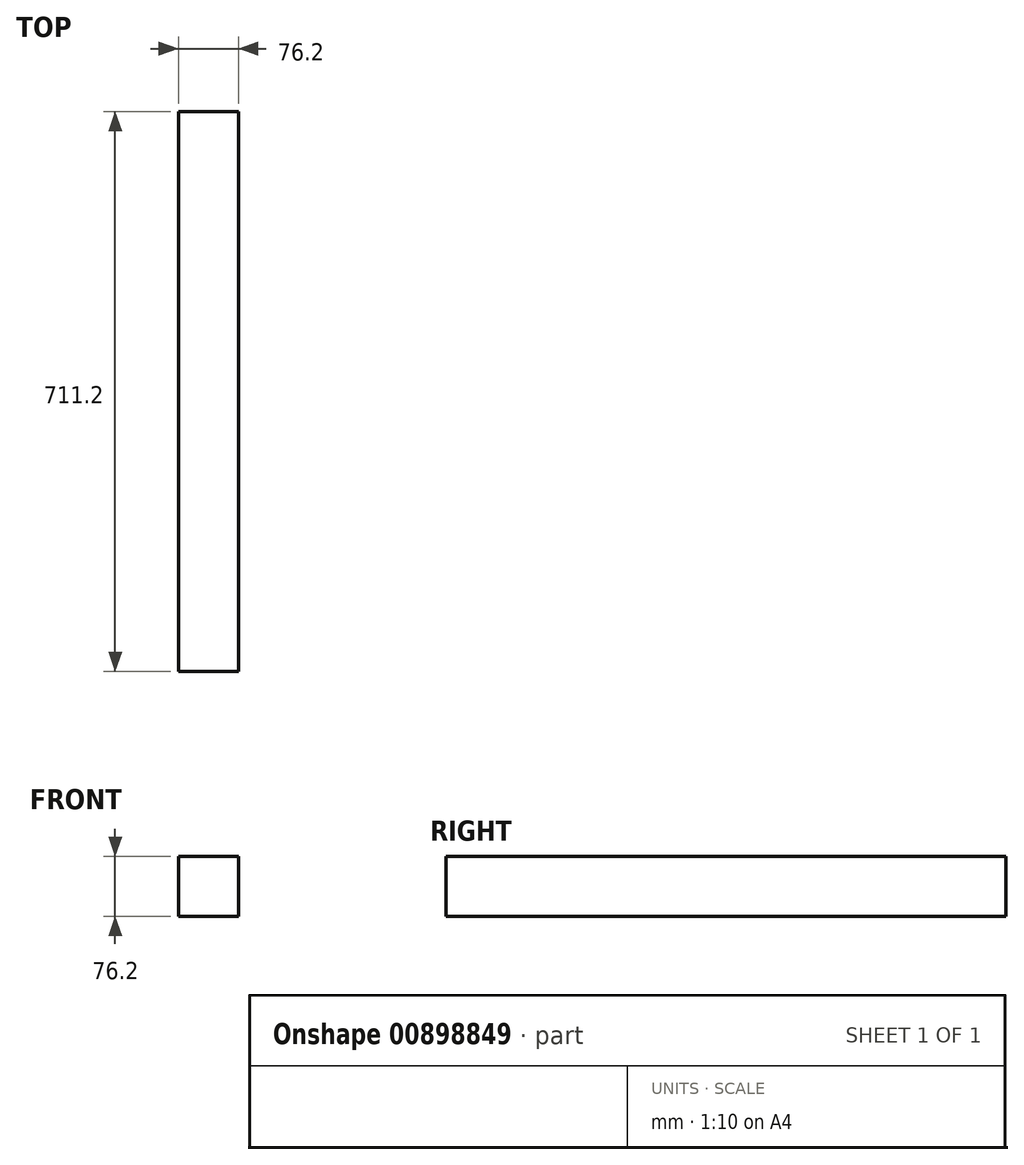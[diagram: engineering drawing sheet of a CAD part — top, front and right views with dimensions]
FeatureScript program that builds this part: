
annotation { "Feature Type Name" : "Feature", "Feature Type Description" : "" }
export const myFeature = defineFeature(function(context is Context, id is Id, definition is map)
    precondition{}
    {
        {
            var Q0;
            Q0=qCreatedBy(makeId("Front.planeOp"),FACE);
            var sketch = newSketch(context, id + "F0", { "sketchPlane" : qUnion([Q0])});
            skLineSegment(sketch, "E0.bottom", {"start": v(0, 0) * mm, "end": v(76.2, 0) * mm});
            skLineSegment(sketch, "E0.top", {"start": v(0, -76.2) * mm, "end": v(76.2, -76.2) * mm});
            skLineSegment(sketch, "E0.left", {"start": v(0, 0) * mm, "end": v(0, -76.2) * mm});
            skLineSegment(sketch, "E0.right", {"start": v(76.2, 0) * mm, "end": v(76.2, -76.2) * mm});
            skSolve(sketch);
        }
        {
            var Q0;
            Q0 = qSketchRegion(id + "F0", true);
            extrude(context, id + "F1", {"entities" : qUnion([Q0]), "depth" : 711.2 * mm, "offsetDistance" : 25.4 * mm});
        }
    });
